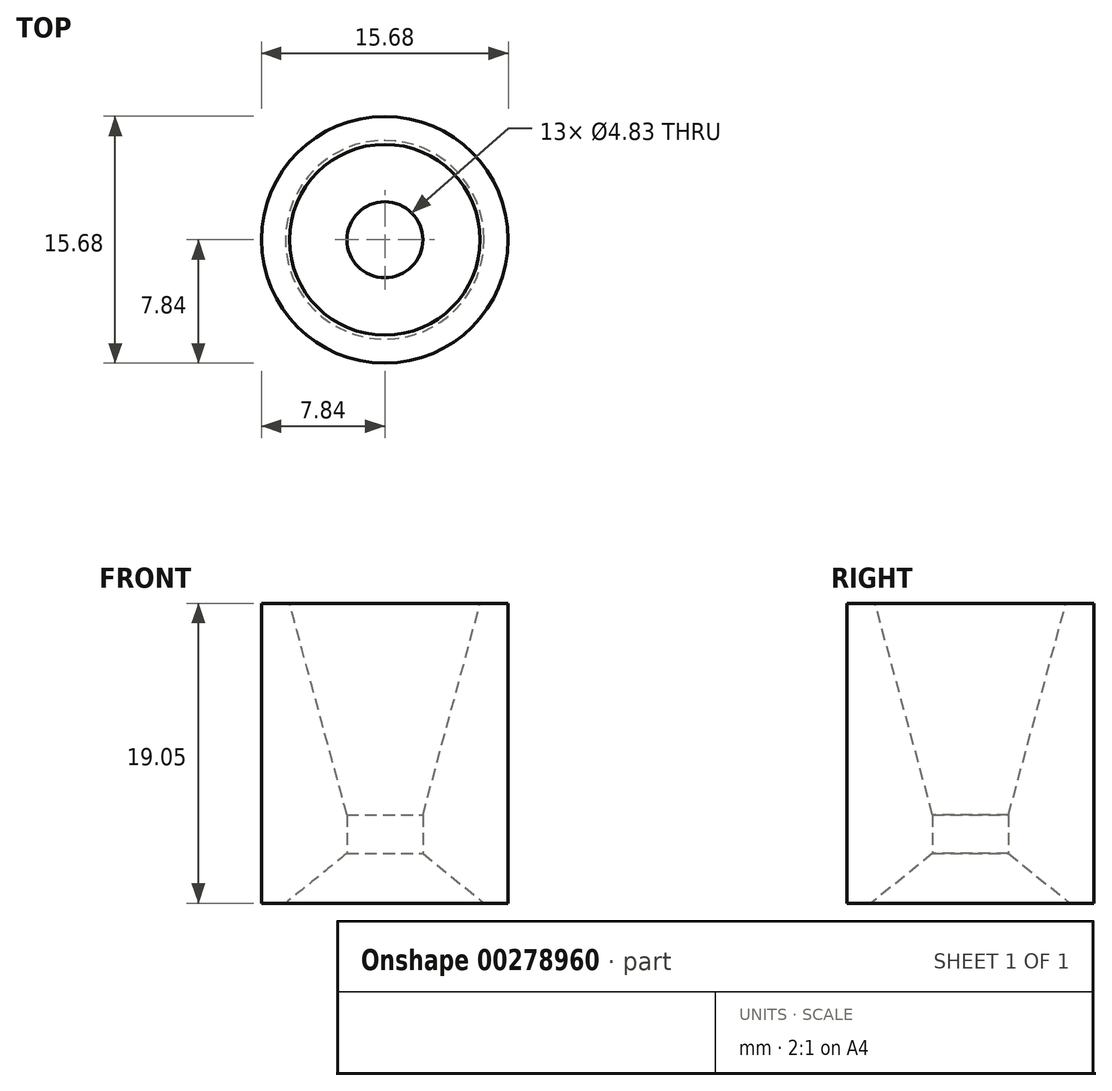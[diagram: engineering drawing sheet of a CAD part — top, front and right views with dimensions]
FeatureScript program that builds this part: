
annotation { "Feature Type Name" : "Feature", "Feature Type Description" : "" }
export const myFeature = defineFeature(function(context is Context, id is Id, definition is map)
    precondition{}
    {
        {
            var Q0;
            Q0=qCreatedBy(makeId("Front.planeOp"),FACE);
            var sketch = newSketch(context, id + "F0", { "sketchPlane" : qUnion([Q0])});
            skLineSegment(sketch, "E0", {"start": v(6.31, 0) * mm, "end": v(7.84, 0) * mm});
            skLineSegment(sketch, "E1", {"start": v(7.84, 0) * mm, "end": v(7.84, 19.05) * mm});
            skLineSegment(sketch, "E2", {"start": v(7.84, 19.05) * mm, "end": v(6.06, 19.05) * mm});
            skLineSegment(sketch, "E3", {"start": v(6.06, 19.05) * mm, "end": v(2.41, 5.6) * mm});
            skLineSegment(sketch, "E4", {"start": v(2.41, 5.6) * mm, "end": v(2.41, 3.16) * mm});
            skLineSegment(sketch, "E5", {"start": v(2.41, 3.16) * mm, "end": v(6.31, 0) * mm});
            skLineSegment(sketch, "E6", {"start": v(0, 0) * mm, "end": v(0, 19.05) * mm, "construction": true});
            skSolve(sketch);
        }
        {
            var Q0;
            Q0 = qSketchRegion(id + "F0", true);
            var Q1;
            Q1=sQuery(id+"F0.wireOp",EDGE,"E6");
            revolve(context, id + "F1", {"entities" : qUnion([Q0]), "axis" : qUnion([Q1]), "revolveType" : RevolveType.FULL});
        }
    });
